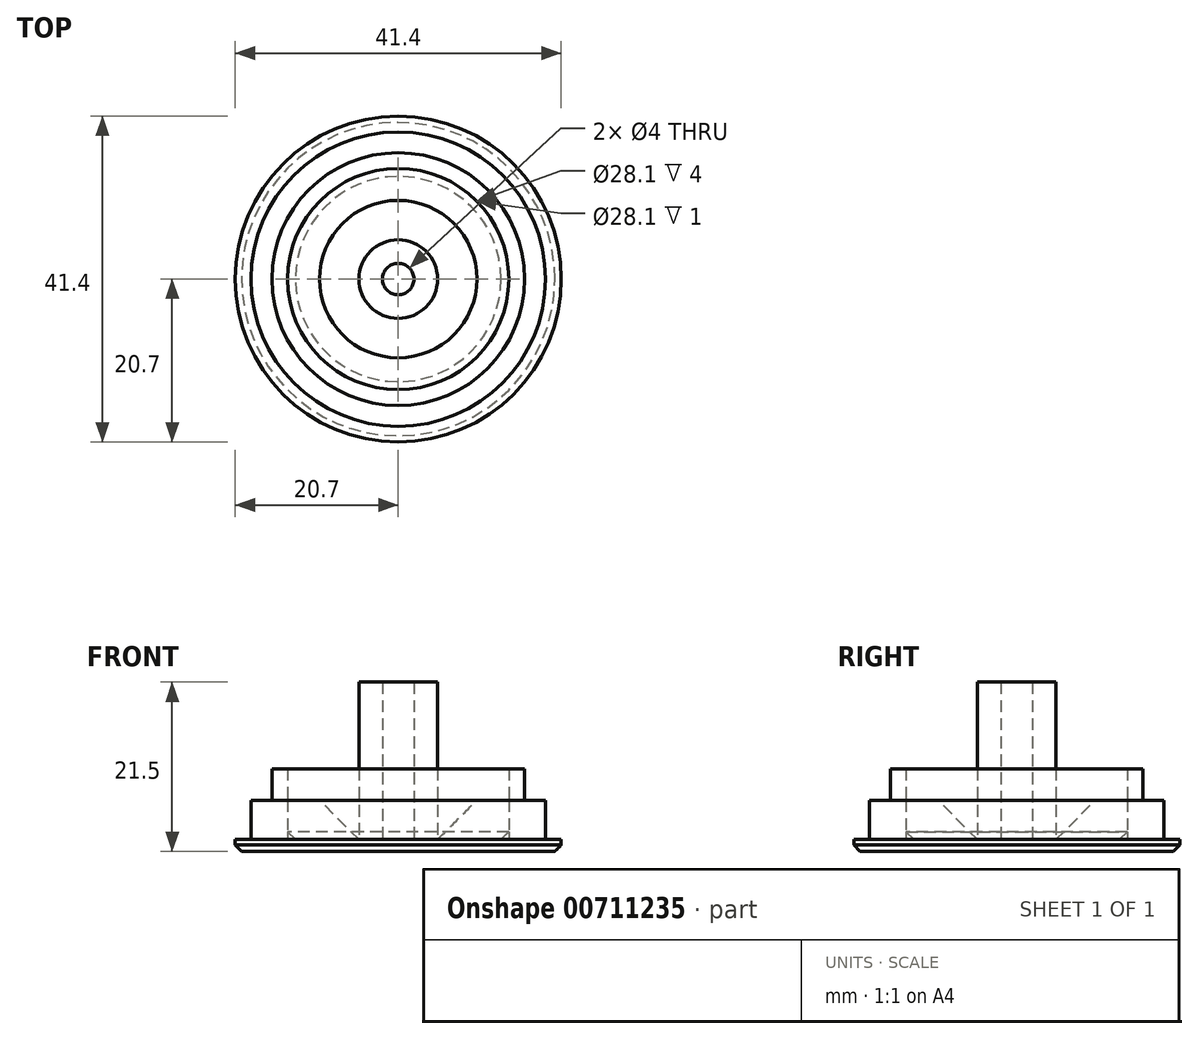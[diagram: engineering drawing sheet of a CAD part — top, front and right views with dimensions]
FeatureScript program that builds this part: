
annotation { "Feature Type Name" : "Feature", "Feature Type Description" : "" }
export const myFeature = defineFeature(function(context is Context, id is Id, definition is map)
    precondition{}
    {
        {
            var Q0;
            Q0=qCreatedBy(makeId("Top.planeOp"),FACE);
            var sketch = newSketch(context, id + "F0", { "sketchPlane" : qUnion([Q0])});
            skCircle(sketch, "E0", {"center": v(0, 0) * mm, "radius": 18.7 * mm});
            skCircle(sketch, "E1", {"center": v(0, 0) * mm, "radius": 16.05 * mm});
            skCircle(sketch, "E2", {"center": v(0, 0) * mm, "radius": 20.7 * mm});
            skCircle(sketch, "E3", {"center": v(0, 0) * mm, "radius": 14.05 * mm});
            skCircle(sketch, "E4", {"center": v(0, 0) * mm, "radius": 5 * mm});
            skCircle(sketch, "E5", {"center": v(0, 0) * mm, "radius": 2 * mm});
            skSolve(sketch);
        }
        {
            var Q0;
            Q0=makeQuery(id+"F0.imprint","IMPRINT",FACE,{"disambiguationData":[TD([[makeQuery(id+"F0.imprint","IMPRINT",EDGE,{"derivedFrom":sQuery(id+"F0.wireOp",EDGE,"E0")}),-1.0]])]});
            var Q1;
            Q1=makeQuery(id+"F0.imprint","IMPRINT",FACE,{"disambiguationData":[TD([[makeQuery(id+"F0.imprint","IMPRINT",EDGE,{"derivedFrom":sQuery(id+"F0.wireOp",EDGE,"E0")}),1.0]])]});
            var Q2;
            Q2=makeQuery(id+"F0.imprint","IMPRINT",FACE,{"disambiguationData":[TD([[makeQuery(id+"F0.imprint","IMPRINT",EDGE,{"derivedFrom":sQuery(id+"F0.wireOp",EDGE,"E1")}),1.0]])]});
            var Q3;
            Q3=makeQuery(id+"F0.imprint","IMPRINT",FACE,{"disambiguationData":[TD([[makeQuery(id+"F0.imprint","IMPRINT",EDGE,{"derivedFrom":sQuery(id+"F0.wireOp",EDGE,"E3")}),1.0]])]});
            var Q4;
            Q4=makeQuery(id+"F0.imprint","IMPRINT",FACE,{"disambiguationData":[TD([[makeQuery(id+"F0.imprint","IMPRINT",EDGE,{"derivedFrom":sQuery(id+"F0.wireOp",EDGE,"E4")}),1.0]])]});
            var Q5;
            Q5=makeQuery(id+"F0.imprint","IMPRINT",FACE,{"disambiguationData":[TD([[makeQuery(id+"F0.imprint","IMPRINT",EDGE,{"derivedFrom":sQuery(id+"F0.wireOp",EDGE,"E5")}),1.0]])]});
            extrude(context, id + "F1", {"entities" : qUnion([Q0, Q1, Q2, Q3, Q4, Q5]), "oppositeDirection" : true, "depth" : 1.5 * mm, "offsetDistance" : 25 * mm});
        }
        {
            var Q0;
            Q0=makeQuery(id+"F0.imprint","IMPRINT",FACE,{"disambiguationData":[TD([[makeQuery(id+"F0.imprint","IMPRINT",EDGE,{"derivedFrom":sQuery(id+"F0.wireOp",EDGE,"E1")}),1.0]])]});
            extrude(context, id + "F2", {"entities" : qUnion([Q0]), "operationType" : NewBodyOperationType.ADD, "depth" : 9 * mm, "offsetDistance" : 25 * mm});
        }
        {
            var Q0;
            Q0=makeQuery(id+"F0.imprint","IMPRINT",FACE,{"disambiguationData":[TD([[makeQuery(id+"F0.imprint","IMPRINT",EDGE,{"derivedFrom":sQuery(id+"F0.wireOp",EDGE,"E0")}),1.0]])]});
            extrude(context, id + "F3", {"entities" : qUnion([Q0]), "operationType" : NewBodyOperationType.ADD, "depth" : 5 * mm, "offsetDistance" : 25 * mm});
        }
        {
            var Q0;
            Q0=makeQuery(id+"F1.opExtrude","CAP_EDGE",EDGE,{"disambiguationData":[OSD([sQuery(id+"F0.wireOp",EDGE,"E2")])],"isStart":false});
            chamfer(context, id + "F4", {"entities" : qUnion([Q0]), "width" : .8 * mm, "tangentPropagation" : true});
        }
        {
            var Q0;
            Q0=makeQuery(id+"F0.imprint","IMPRINT",FACE,{"disambiguationData":[TD([[makeQuery(id+"F0.imprint","IMPRINT",EDGE,{"derivedFrom":sQuery(id+"F0.wireOp",EDGE,"E4")}),1.0]])]});
            extrude(context, id + "F5", {"entities" : qUnion([Q0]), "depth" : 20 * mm, "offsetDistance" : 25 * mm});
        }
        {
            var Q0;
            Q0=makeQuery(id+"F0.imprint","IMPRINT",FACE,{"disambiguationData":[TD([[makeQuery(id+"F0.imprint","IMPRINT",EDGE,{"derivedFrom":sQuery(id+"F0.wireOp",EDGE,"E3")}),1.0]])]});
            extrude(context, id + "F6", {"entities" : qUnion([Q0]), "depth" : 5 * mm, "offsetDistance" : 25 * mm});
        }
        {
            var Q0;
            Q0=makeQuery(id+"F6.opExtrude","CAP_EDGE",EDGE,{"disambiguationData":[OSD([sQuery(id+"F0.wireOp",EDGE,"E3")])],"isStart":true});
            chamfer(context, id + "F7", {"entities" : qUnion([Q0]), "width" : 1 * mm, "tangentPropagation" : true});
        }
        {
            var Q0;
            Q0=makeQuery(id+"F6.opExtrude","CAP_EDGE",EDGE,{"disambiguationData":[OSD([sQuery(id+"F0.wireOp",EDGE,"E4")])],"isStart":false});
            chamfer(context, id + "F8", {"entities" : qUnion([Q0]), "width" : 5 * mm, "tangentPropagation" : true});
        }
    });
